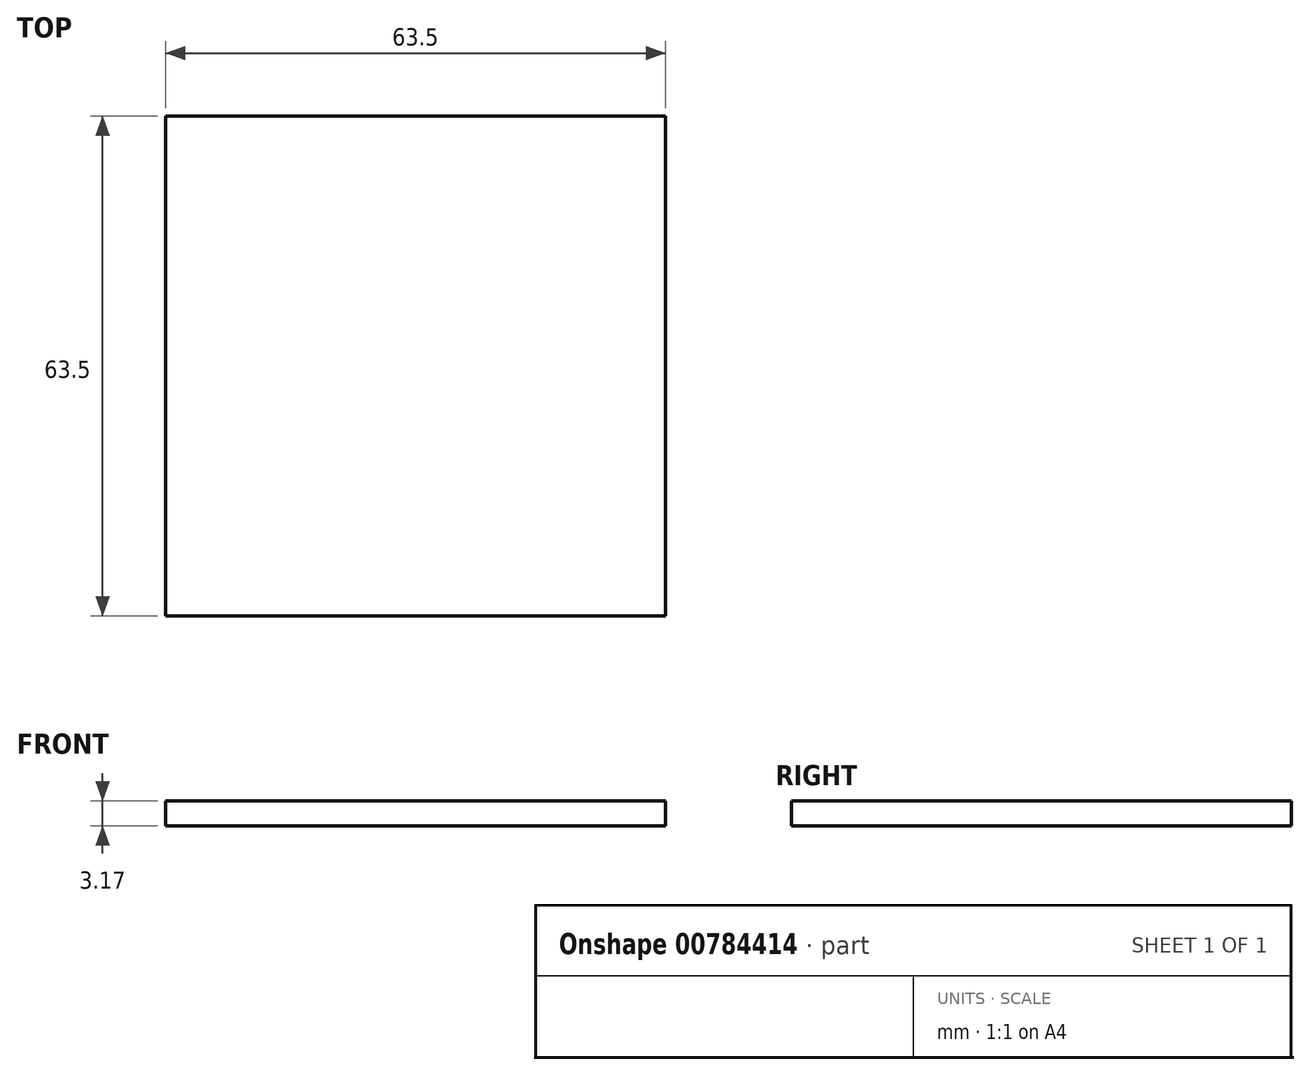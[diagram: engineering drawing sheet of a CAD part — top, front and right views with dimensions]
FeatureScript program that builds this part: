
annotation { "Feature Type Name" : "Feature", "Feature Type Description" : "" }
export const myFeature = defineFeature(function(context is Context, id is Id, definition is map)
    precondition{}
    {
        {
            var Q0;
            Q0=qCreatedBy(makeId("Top.planeOp"),FACE);
            var sketch = newSketch(context, id + "F0", { "sketchPlane" : qUnion([Q0])});
            skLineSegment(sketch, "E0.bottom", {"start": v(-32.8, 28.07) * mm, "end": v(30.7, 28.07) * mm});
            skLineSegment(sketch, "E0.top", {"start": v(-32.8, -35.43) * mm, "end": v(30.7, -35.43) * mm});
            skLineSegment(sketch, "E0.left", {"start": v(-32.8, 28.07) * mm, "end": v(-32.8, -35.43) * mm});
            skLineSegment(sketch, "E0.right", {"start": v(30.7, 28.07) * mm, "end": v(30.7, -35.43) * mm});
            skSolve(sketch);
        }
        {
            var Q0;
            Q0=makeQuery(id+"F0.imprint","IMPRINT",FACE,{"disambiguationData":[TD([[makeQuery(id+"F0.imprint","IMPRINT",EDGE,{"derivedFrom":sQuery(id+"F0.wireOp",EDGE,"E0.bottom")}),-1.0]])]});
            extrude(context, id + "F1", {"entities" : qUnion([Q0]), "depth" : 3.17 * mm, "offsetDistance" : 25.4 * mm});
        }
    });
